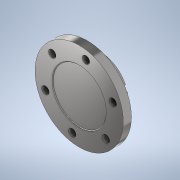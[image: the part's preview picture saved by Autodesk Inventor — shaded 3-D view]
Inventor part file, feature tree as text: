
AUTODESK INVENTOR PART (.ipt)
format: ipt  version: 2020 (Build 240168000, 168)  size: 176,128 bytes
history: native  units: mm
features: extrude x4, sketch x4, reference x4, other x4, plane x2, fillet x1
ambient origin geometry x8: Origin, YZ Plane, XZ Plane, XY Plane, X Axis, Y Axis, Z Axis, Center Point
bodies: 实体1 (feature_tree)
feature tree (19):
  plane  "工作平面1"
  extrude  "拉伸1"  Depth=12.0mm
  extrude  "拉伸2"  Depth=20.0mm TaperAngle=0.0deg
  extrude  "拉伸3"  Depth=1.0mm TaperAngle=0.0deg
  fillet  "圆角1"  Radius=1.0mm
  extrude  "拉伸4"  Depth=8.0mm TaperAngle=0.0deg
  plane  "工作平面2"
  sketch  "草图1"  dims[d0=12.0mm d1=0.0mm d2=80.0mm]
  reference  "参考1"
  reference  "参考2"
  reference  "参考3"
  sketch  "草图2"  dims[d3=70.0mm d4=20.0mm d5=0.0mm]
  reference  "参考4"
  sketch  "草图3"  dims[d6=80.0mm d7=1.0mm d8=0.0mm d9=1.0mm]
  sketch  "草图4"  dims[d10=8.0mm d11=8.0mm d12=0.0mm]
  other  "<userpath>\Desktop\ME_course_project\课设试试\shaft_try_1.iam"
  other  "shaft_try_1.iam"
  other  "xia(1):1"
  other  "轴承端盖1:1"
